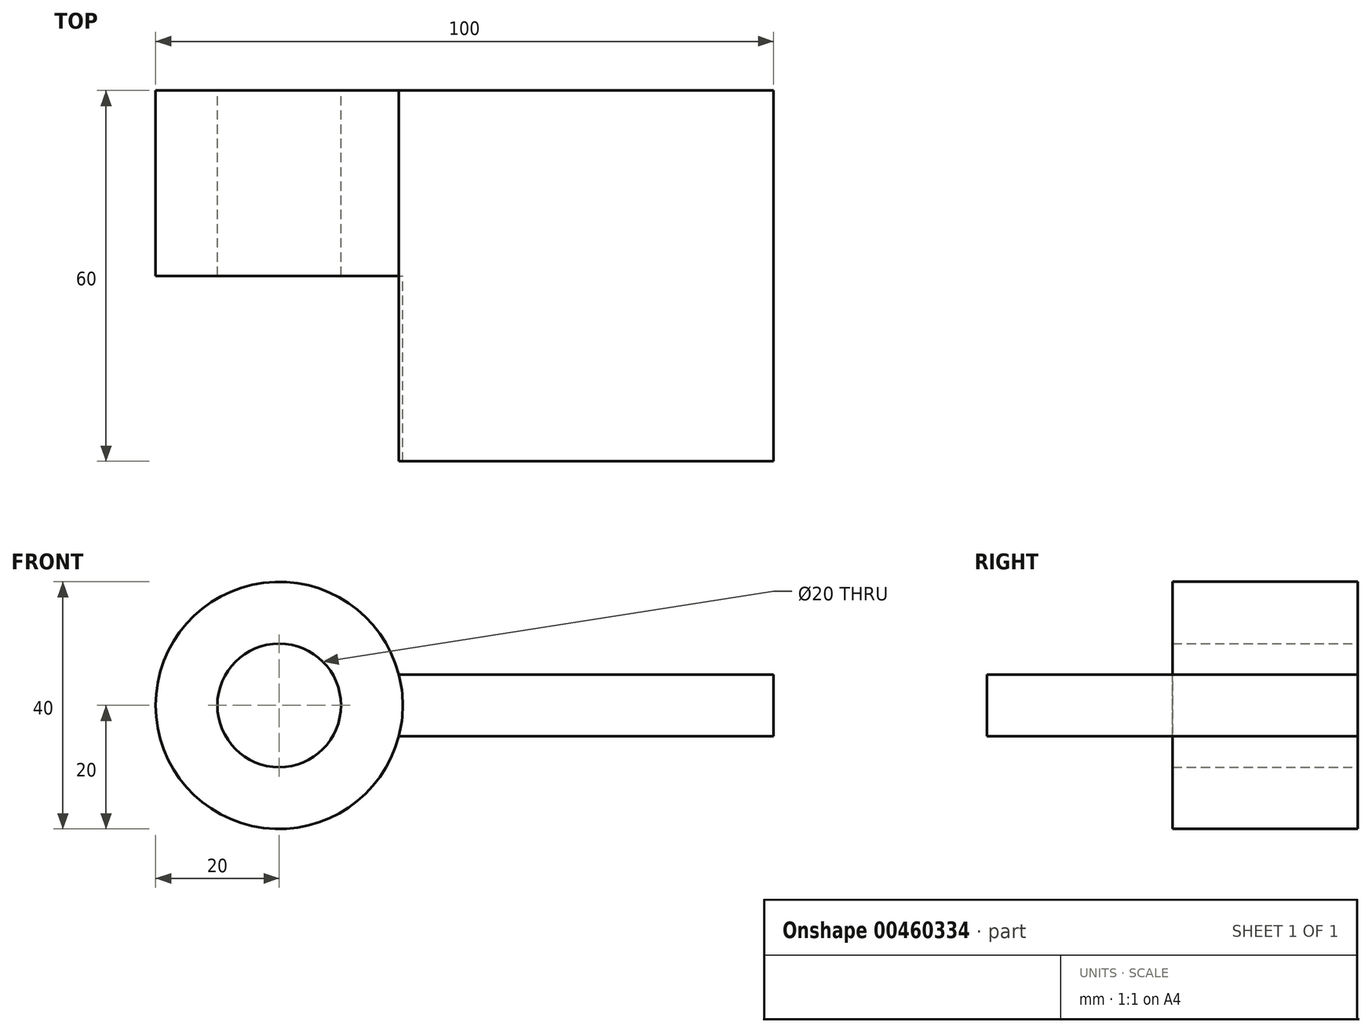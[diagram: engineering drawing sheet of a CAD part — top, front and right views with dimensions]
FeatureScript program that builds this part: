
annotation { "Feature Type Name" : "Feature", "Feature Type Description" : "" }
export const myFeature = defineFeature(function(context is Context, id is Id, definition is map)
    precondition{}
    {
        {
            var Q0;
            Q0=qCreatedBy(makeId("Front.planeOp"),FACE);
            var sketch = newSketch(context, id + "F0", { "sketchPlane" : qUnion([Q0])});
            skCircle(sketch, "E0", {"center": v(0, 0) * mm, "radius": 20 * mm});
            skCircle(sketch, "E1", {"center": v(0, 0) * mm, "radius": 10 * mm});
            skLineSegment(sketch, "E2", {"start": v(0, 0) * mm, "end": v(80, 0) * mm});
            skLineSegment(sketch, "E3", {"start": v(80, 0) * mm, "end": v(80, 5) * mm});
            skLineSegment(sketch, "E4", {"start": v(80, 0) * mm, "end": v(80, -5) * mm});
            skLineSegment(sketch, "E5", {"start": v(80, 5) * mm, "end": v(19.36, 5) * mm});
            skLineSegment(sketch, "E6", {"start": v(80, -5) * mm, "end": v(19.36, -5) * mm});
            skSolve(sketch);
        }
        {
            var Q0;
            Q0=makeQuery(id+"F0.imprint","IMPRINT",FACE,{"disambiguationData":[TD([[makeQuery(id+"F0.imprint","IMPRINT",EDGE,{"derivedFrom":sQuery(id+"F0.wireOp",EDGE,"E1")}),-1.0]])]});
            extrude(context, id + "F1", {"entities" : qUnion([Q0]), "depth" : 30 * mm});
        }
        {
            var Q0;
            {var subQ4=sQuery(id+"F0.wireOp",EDGE,"E3");Q0=makeQuery(id+"F0.imprint","IMPRINT",FACE,{"disambiguationData":[TD([[makeQuery(id+"F0.imprint","IMPRINT",EDGE,{"derivedFrom":subQ4}),1.0]])]});}
            var Q1;
            {var subQ4=sQuery(id+"F0.wireOp",EDGE,"E4");Q1=makeQuery(id+"F0.imprint","IMPRINT",FACE,{"disambiguationData":[TD([[makeQuery(id+"F0.imprint","IMPRINT",EDGE,{"derivedFrom":subQ4}),-1.0]])]});}
            extrude(context, id + "F2", {"entities" : qUnion([Q0, Q1]), "operationType" : NewBodyOperationType.ADD, "depth" : 60 * mm});
        }
    });
